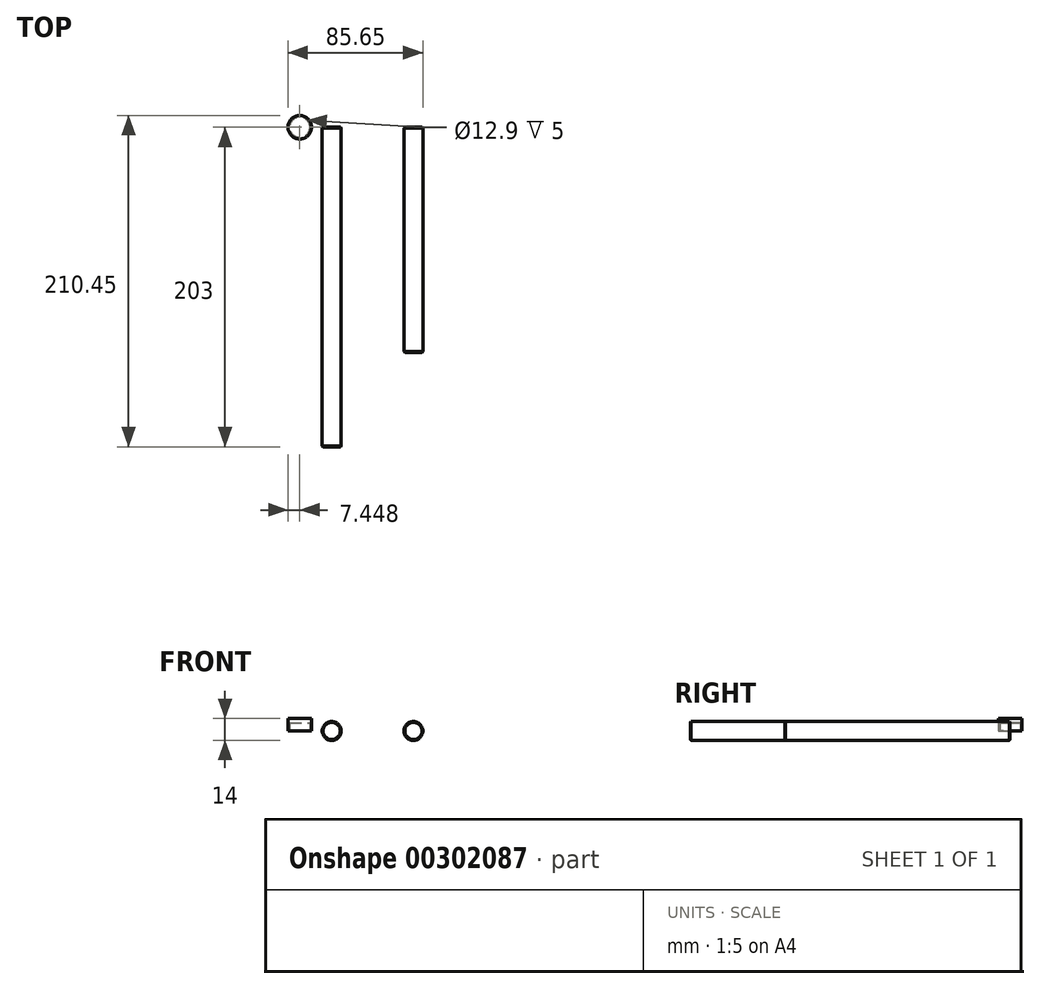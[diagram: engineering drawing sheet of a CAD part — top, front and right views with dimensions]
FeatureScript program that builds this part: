
annotation { "Feature Type Name" : "Feature", "Feature Type Description" : "" }
export const myFeature = defineFeature(function(context is Context, id is Id, definition is map)
    precondition{}
    {
        {
            var Q0;
            Q0=qCreatedBy(makeId("Front.planeOp"),FACE);
            var sketch = newSketch(context, id + "F0", { "sketchPlane" : qUnion([Q0])});
            skCircle(sketch, "E0", {"center": v(0, 0) * mm, "radius": 6 * mm});
            skCircle(sketch, "E1", {"center": v(51.95, 0) * mm, "radius": 6 * mm});
            skSolve(sketch);
        }
        {
            var Q0;
            Q0=makeQuery(id+"F0.imprint","IMPRINT",FACE,{"disambiguationData":[TD([[makeQuery(id+"F0.imprint","IMPRINT",EDGE,{"derivedFrom":sQuery(id+"F0.wireOp",EDGE,"E0")}),1.0]])]});
            extrude(context, id + "F1", {"entities" : qUnion([Q0]), "depth" : 203 * mm});
        }
        {
            var Q0;
            Q0=makeQuery(id+"F1.opExtrude","CAP_EDGE",EDGE,{"disambiguationData":[OSD([sQuery(id+"F0.wireOp",EDGE,"E0")])],"isStart":false});
            var Q1;
            Q1=makeQuery(id+"F1.opExtrude","CAP_EDGE",EDGE,{"disambiguationData":[OSD([sQuery(id+"F0.wireOp",EDGE,"E0")])],"isStart":true});
            chamfer(context, id + "F2", {"entities" : qUnion([Q0, Q1]), "width" : 0.5 * mm, "tangentPropagation" : true});
        }
        {
            var Q0;
            Q0=makeQuery(id+"F0.imprint","IMPRINT",FACE,{"disambiguationData":[TD([[makeQuery(id+"F0.imprint","IMPRINT",EDGE,{"derivedFrom":sQuery(id+"F0.wireOp",EDGE,"E1")}),1.0]])]});
            var Q1;
            Q1=sQuery(id+"F0.wireOp",EDGE,"E1");
            extrude(context, id + "F3", {"entities" : qUnion([Q0]), "surfaceEntities" : qUnion([Q1]), "depth" : 143 * mm});
        }
        {
            var Q0;
            Q0=makeQuery(id+"F3.opExtrude","CAP_EDGE",EDGE,{"disambiguationData":[OSD([sQuery(id+"F0.wireOp",EDGE,"E1")])],"isStart":false});
            var Q1;
            Q1=makeQuery(id+"F3.opExtrude","CAP_EDGE",EDGE,{"disambiguationData":[OSD([sQuery(id+"F0.wireOp",EDGE,"E1")])],"isStart":true});
            chamfer(context, id + "F4", {"entities" : qUnion([Q0, Q1]), "width" : 0.5 * mm, "tangentPropagation" : true});
        }
        {
            var Q0;
            Q0=qCreatedBy(makeId("Top.planeOp"),FACE);
            var sketch = newSketch(context, id + "F5", { "sketchPlane" : qUnion([Q0])});
            skCircle(sketch, "E2", {"center": v(-20.25, 0) * mm, "radius": 7.45 * mm});
            skSolve(sketch);
        }
        {
            var Q0;
            Q0=makeQuery(id+"F5.imprint","IMPRINT",FACE,{"disambiguationData":[TD([[makeQuery(id+"F5.imprint","IMPRINT",EDGE,{"derivedFrom":sQuery(id+"F5.wireOp",EDGE,"E2")}),1.0]])]});
            extrude(context, id + "F6", {"entities" : qUnion([Q0]), "depth" : 8 * mm});
        }
        {
            var Q0;
            Q0=makeQuery(id+"F6.opExtrude","CAP_FACE",FACE,{"disambiguationData":[OSD([sQuery(id+"F5.wireOp",EDGE,"E2")])],"isStart":true});
            var sketch = newSketch(context, id + "F7", { "sketchPlane" : qUnion([Q0])});
            skPoint(sketch, "E3", {"position": v(-20.25, 0) * mm});
            skCircle(sketch, "E4", {"center": v(-20.25, 0) * mm, "radius": 6.45 * mm});
            skSolve(sketch);
        }
        {
            var Q0;
            Q0=makeQuery(id+"F7.imprint","IMPRINT",FACE,{"disambiguationData":[TD([[makeQuery(id+"F7.imprint","IMPRINT",EDGE,{"derivedFrom":sQuery(id+"F7.wireOp",EDGE,"E4")}),1.0]])]});
            extrude(context, id + "F8", {"entities" : qUnion([Q0]), "operationType" : NewBodyOperationType.REMOVE, "oppositeDirection" : true, "depth" : 5 * mm});
        }
    });
